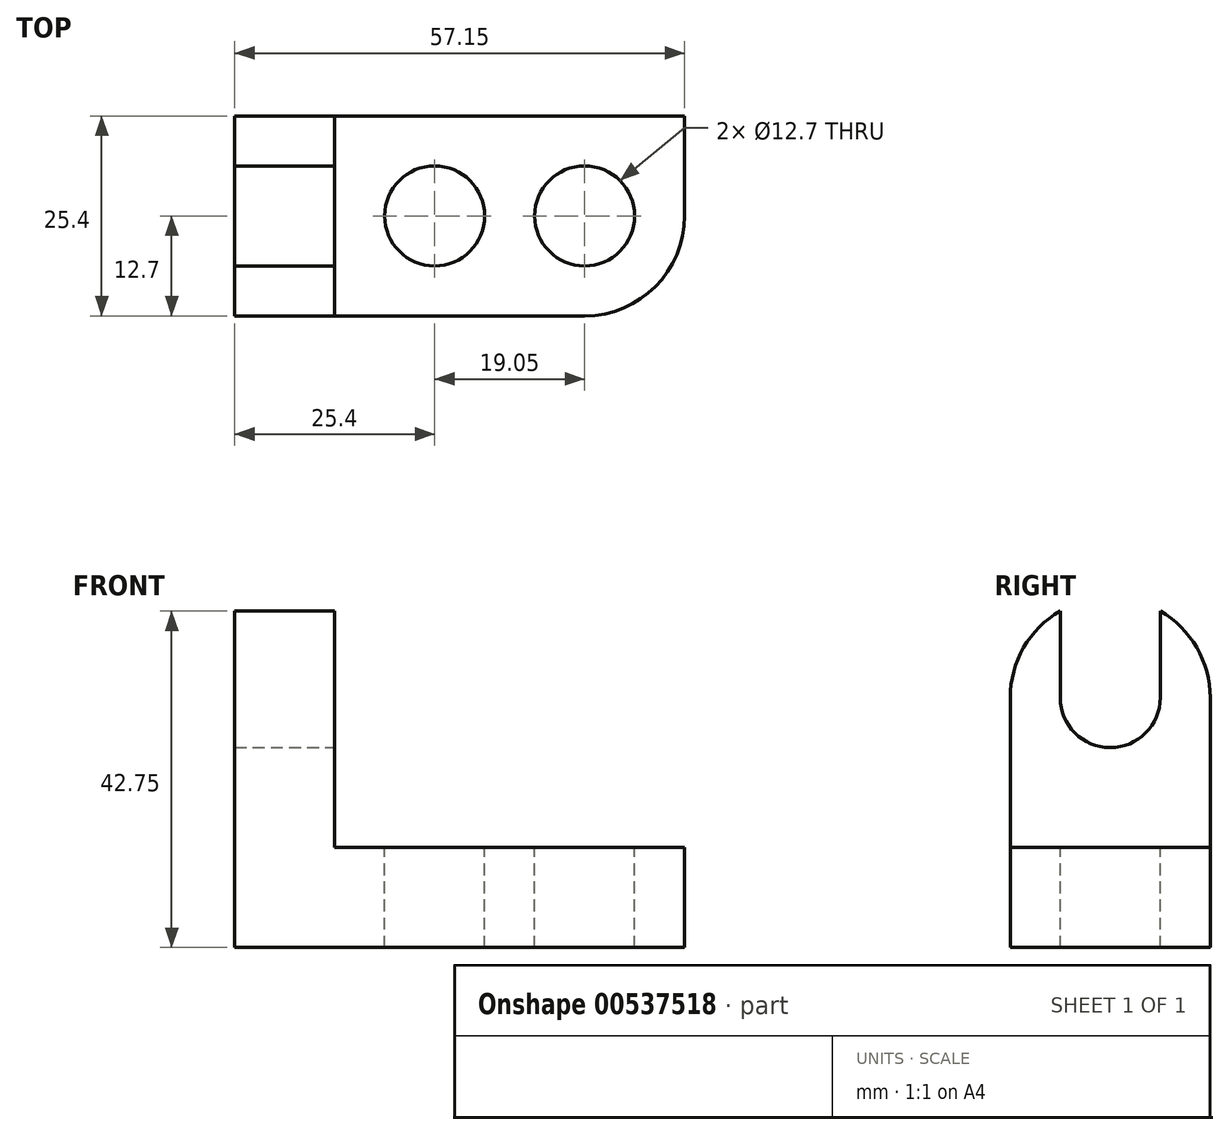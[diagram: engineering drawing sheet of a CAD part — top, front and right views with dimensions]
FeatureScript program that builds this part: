
annotation { "Feature Type Name" : "Feature", "Feature Type Description" : "" }
export const myFeature = defineFeature(function(context is Context, id is Id, definition is map)
    precondition{}
    {
        {
            var Q0;
            Q0=qCreatedBy(makeId("Front.planeOp"),FACE);
            var sketch = newSketch(context, id + "F0", { "sketchPlane" : qUnion([Q0])});
            skLineSegment(sketch, "E0", {"start": v(0, 0) * mm, "end": v(57.15, 0) * mm});
            skLineSegment(sketch, "E1", {"start": v(57.15, 0) * mm, "end": v(57.15, 44.45) * mm});
            skLineSegment(sketch, "E2", {"start": v(57.15, 44.45) * mm, "end": v(0, 44.45) * mm});
            skLineSegment(sketch, "E3", {"start": v(0, 44.45) * mm, "end": v(0, 0) * mm});
            skSolve(sketch);
        }
        {
            var Q0;
            Q0 = qSketchRegion(id + "F0", true);
            extrude(context, id + "F1", {"entities" : qUnion([Q0]), "depth" : 25.4 * mm, "offsetDistance" : 25.4 * mm});
        }
        {
            var Q0;
            Q0=makeQuery(id+"F1.opExtrude","CAP_FACE",FACE,{"disambiguationData":[OSD([sQuery(id+"F0.wireOp",EDGE,"E0"),sQuery(id+"F0.wireOp",EDGE,"E1"),sQuery(id+"F0.wireOp",EDGE,"E2"),sQuery(id+"F0.wireOp",EDGE,"E3")])],"isStart":false});
            var sketch = newSketch(context, id + "F2", { "sketchPlane" : qUnion([Q0])});
            skLineSegment(sketch, "E4", {"start": v(0, 44.45) * mm, "end": v(12.7, 44.45) * mm});
            skLineSegment(sketch, "E5", {"start": v(12.7, 44.45) * mm, "end": v(12.7, 12.7) * mm});
            skLineSegment(sketch, "E6", {"start": v(12.7, 12.7) * mm, "end": v(57.15, 12.7) * mm});
            skSolve(sketch);
        }
        {
            var Q0;
            Q0 = qSketchRegion(id + "F2", true);
            var Q1;
            {var subQ0=sQuery(id+"F2.wireOp",EDGE,"E5");Q1=makeQuery(id+"F2.imprint","IMPRINT",FACE,{"disambiguationData":[TD([[makeQuery(id+"F2.imprint","IMPRINT",EDGE,{"derivedFrom":subQ0}),1.0]])]});}
            extrude(context, id + "F3", {"entities" : qUnion([Q0, Q1]), "operationType" : NewBodyOperationType.REMOVE, "oppositeDirection" : true, "depth" : 25.4 * mm, "offsetDistance" : 25.4 * mm});
        }
        {
            var Q0;
            Q0=makeQuery(id+"F3.boolean.opBoolean","COPY",FACE,{"derivedFrom":makeQuery(id+"F3.opExtrude","SWEPT_FACE",FACE,{"disambiguationData":[OSD([sQuery(id+"F2.wireOp",EDGE,"E6")])]})});
            var sketch = newSketch(context, id + "F4", { "sketchPlane" : qUnion([Q0])});
            skCircle(sketch, "E7", {"center": v(25.4, -12.7) * mm, "radius": 6.35 * mm});
            skCircle(sketch, "E8", {"center": v(44.45, -12.7) * mm, "radius": 6.35 * mm});
            skArc(sketch, "E9", {"start": v(44.45, -25.4) * mm, "mid": v(57.15, -12.7) * mm, "end": v(44.45, 0) * mm});
            skLineSegment(sketch, "E10", {"start": v(57.15, -12.7) * mm, "end": v(57.15, -25.4) * mm});
            skSolve(sketch);
        }
        {
            var Q0;
            {var subQ3=sQuery(id+"F4.wireOp",EDGE,"E10");Q0=makeQuery(id+"F4.imprint","IMPRINT",FACE,{"disambiguationData":[TD([[makeQuery(id+"F4.imprint","IMPRINT",EDGE,{"derivedFrom":subQ3}),-1.0]])]});}
            var Q1;
            Q1=makeQuery(id+"F4.imprint","IMPRINT",FACE,{"disambiguationData":[TD([[makeQuery(id+"F4.imprint","IMPRINT",EDGE,{"derivedFrom":sQuery(id+"F4.wireOp",EDGE,"E8")}),1.0]])]});
            var Q2;
            Q2=makeQuery(id+"F4.imprint","IMPRINT",FACE,{"disambiguationData":[TD([[makeQuery(id+"F4.imprint","IMPRINT",EDGE,{"derivedFrom":sQuery(id+"F4.wireOp",EDGE,"E7")}),1.0]])]});
            var Q3;
            {var subQ0=sQuery(id+"F4.wireOp",EDGE,"E9");var subQ1=sQuery(id+"F2.wireOp",EDGE,"E6");var subQ2=makeQuery(id+"F3.boolean.opBoolean","COPY",EDGE,{"derivedFrom":makeQuery(id+"F3.opExtrude","CAP_EDGE",EDGE,{"disambiguationData":[OSD([subQ1])],"isStart":false})});var subQ3=makeQuery(id+"F4.imprint","INTERSECT",VERTEX,{"derivedFrom":[subQ2,subQ0]});Q3=makeQuery(id+"F4.imprint","IMPRINT",FACE,{"disambiguationData":[TD([[makeQuery(id+"F4.imprint","IMPRINT",EDGE,{"disambiguationData":[TD([[subQ3,-1.0]])],"derivedFrom":subQ2}),-1.0]])]});}
            extrude(context, id + "F5", {"entities" : qUnion([Q0, Q1, Q2, Q3]), "operationType" : NewBodyOperationType.REMOVE, "oppositeDirection" : true, "depth" : 12.7 * mm, "offsetDistance" : 25.4 * mm});
        }
        {
            var Q0;
            Q0=makeQuery(id+"F3.boolean.opBoolean","COPY",FACE,{"derivedFrom":makeQuery(id+"F3.opExtrude","SWEPT_FACE",FACE,{"disambiguationData":[OSD([sQuery(id+"F2.wireOp",EDGE,"E5")])]})});
            var sketch = newSketch(context, id + "F6", { "sketchPlane" : qUnion([Q0])});
            skLineSegment(sketch, "E11", {"start": v(-25.4, 44.45) * mm, "end": v(-19.05, 44.45) * mm});
            skLineSegment(sketch, "E12", {"start": v(-19.05, 44.45) * mm, "end": v(-19.05, 31.75) * mm});
            skLineSegment(sketch, "E13", {"start": v(-19.05, 31.75) * mm, "end": v(-6.35, 31.75) * mm});
            skLineSegment(sketch, "E14", {"start": v(-6.35, 31.75) * mm, "end": v(-6.35, 44.45) * mm});
            skLineSegment(sketch, "E15", {"start": v(-6.35, 44.45) * mm, "end": v(0, 44.45) * mm});
            skArc(sketch, "E16", {"start": v(-19.05, 31.75) * mm, "mid": v(-12.7, 25.4) * mm, "end": v(-6.35, 31.75) * mm});
            skPoint(sketch, "E17.startSnap0", {"position": v(-19.05, 38.1) * mm});
            skPoint(sketch, "E17.endSnap0", {"position": v(-19.05, 38.1) * mm});
            skArc(sketch, "E18", {"start": v(0, 31.75) * mm, "mid": v(-12.7, 44.45) * mm, "end": v(-25.4, 31.75) * mm});
            skPoint(sketch, "E18.endSnap0", {"position": v(-25.4, 28.58) * mm});
            skLineSegment(sketch, "E19", {"start": v(-25.4, 44.45) * mm, "end": v(-12.7, 44.45) * mm});
            skSolve(sketch);
        }
        {
            var Q0;
            Q0 = qSketchRegion(id + "F6", true);
            var Q1;
            {var subQ0=sQuery(id+"F6.wireOp",EDGE,"E15");Q1=makeQuery(id+"F6.imprint","IMPRINT",FACE,{"disambiguationData":[TD([[makeQuery(id+"F6.imprint","IMPRINT",EDGE,{"derivedFrom":subQ0}),1.0]])]});}
            var Q2;
            {var subQ0=sQuery(id+"F6.wireOp",EDGE,"E19");var subQ1=sQuery(id+"F6.wireOp",EDGE,"E12");var subQ2=makeQuery(id+"F6.imprint","INTERSECT",VERTEX,{"derivedFrom":[subQ1,subQ0]});Q2=makeQuery(id+"F6.imprint","IMPRINT",FACE,{"disambiguationData":[TD([[makeQuery(id+"F6.imprint","IMPRINT",EDGE,{"disambiguationData":[TD([[subQ2,-1.0]])],"derivedFrom":subQ1}),-1.0]])]});}
            var Q3;
            {var subQ0=sQuery(id+"F6.wireOp",EDGE,"E14");var subQ3=sQuery(id+"F6.wireOp",EDGE,"E18");var subQ4=makeQuery(id+"F6.imprint","INTERSECT",VERTEX,{"derivedFrom":[subQ0,subQ3]});Q3=makeQuery(id+"F6.imprint","IMPRINT",FACE,{"disambiguationData":[TD([[makeQuery(id+"F6.imprint","IMPRINT",EDGE,{"disambiguationData":[TD([[subQ4,-1.0]])],"derivedFrom":subQ0}),1.0]])]});}
            extrude(context, id + "F7", {"entities" : qUnion([Q0, Q1, Q2, Q3]), "operationType" : NewBodyOperationType.REMOVE, "oppositeDirection" : true, "depth" : 12.7 * mm, "offsetDistance" : 25.4 * mm});
        }
    });
